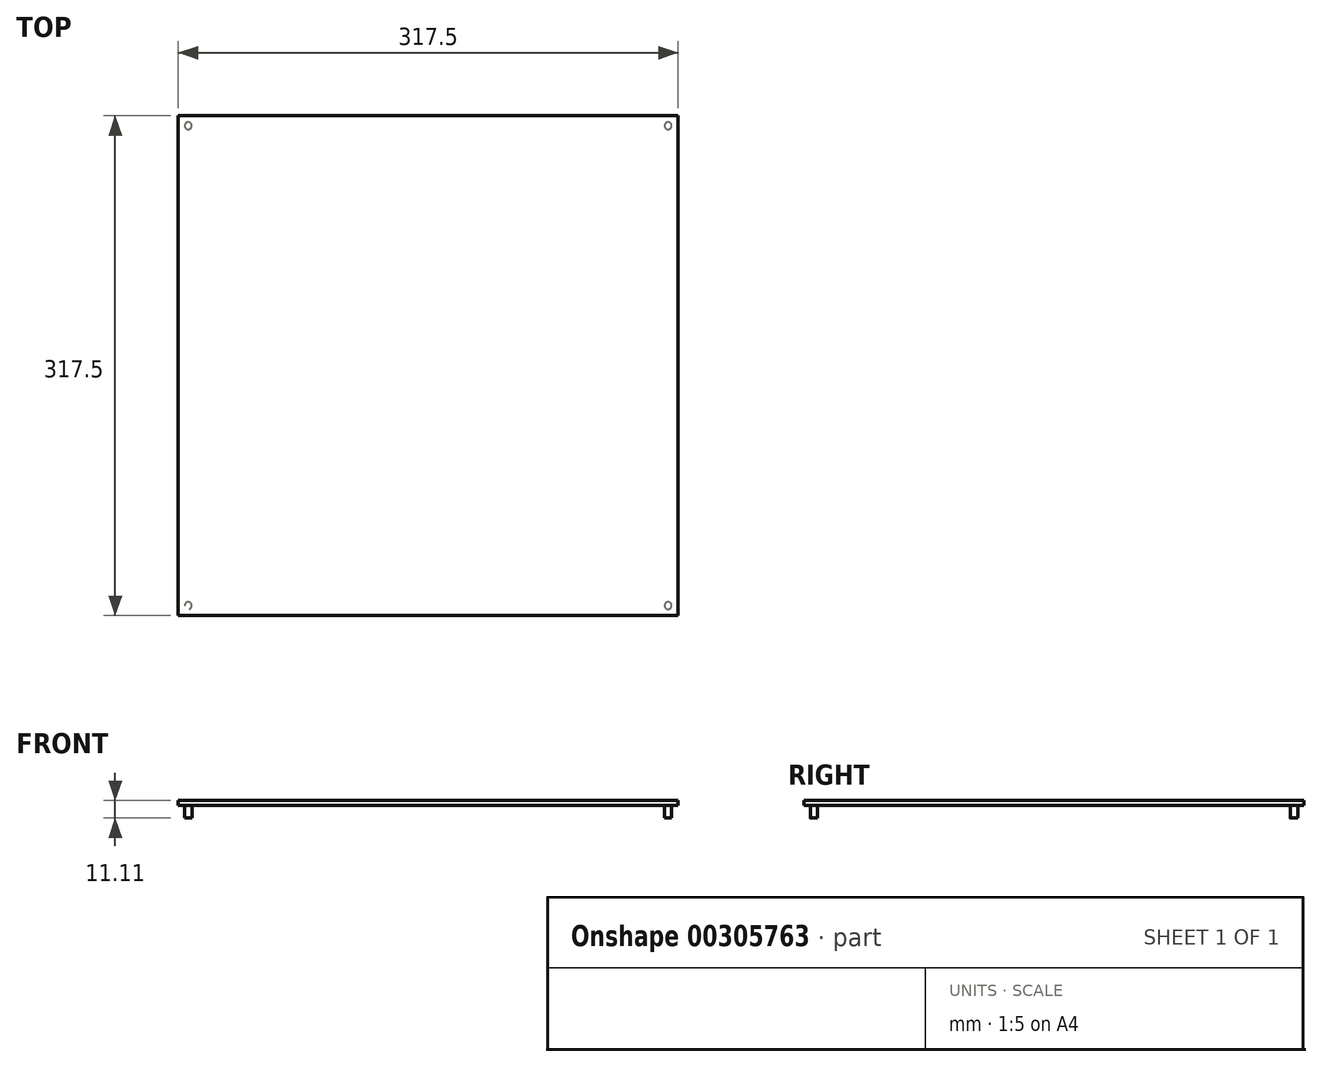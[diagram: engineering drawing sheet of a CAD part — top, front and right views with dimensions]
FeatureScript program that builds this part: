
annotation { "Feature Type Name" : "Feature", "Feature Type Description" : "" }
export const myFeature = defineFeature(function(context is Context, id is Id, definition is map)
    precondition{}
    {
        {
            var Q0;
            Q0=qCreatedBy(makeId("Top.planeOp"),FACE);
            var sketch = newSketch(context, id + "F0", { "sketchPlane" : qUnion([Q0])});
            skLineSegment(sketch, "E0.bottom", {"start": v(-158.75, 158.75) * mm, "end": v(158.75, 158.75) * mm});
            skLineSegment(sketch, "E0.top", {"start": v(-158.75, -158.75) * mm, "end": v(158.75, -158.75) * mm});
            skLineSegment(sketch, "E0.left", {"start": v(-158.75, 158.75) * mm, "end": v(-158.75, -158.75) * mm});
            skLineSegment(sketch, "E0.right", {"start": v(158.75, 158.75) * mm, "end": v(158.75, -158.75) * mm});
            skSolve(sketch);
        }
        {
            var Q0;
            Q0=makeQuery(id+"F0.imprint","IMPRINT",FACE,{"disambiguationData":[TD([[makeQuery(id+"F0.imprint","IMPRINT",EDGE,{"derivedFrom":sQuery(id+"F0.wireOp",EDGE,"E0.bottom")}),-1.0]])]});
            extrude(context, id + "F1", {"entities" : qUnion([Q0]), "depth" : 3.17 * mm});
        }
        {
            var Q0;
            Q0=makeQuery(id+"F1.opExtrude","CAP_FACE",FACE,{"disambiguationData":[OSD([sQuery(id+"F0.wireOp",EDGE,"E0.bottom"),sQuery(id+"F0.wireOp",EDGE,"E0.top"),sQuery(id+"F0.wireOp",EDGE,"E0.left"),sQuery(id+"F0.wireOp",EDGE,"E0.right")])],"isStart":true});
            var sketch = newSketch(context, id + "F2", { "sketchPlane" : qUnion([Q0])});
            skCircle(sketch, "E1", {"center": v(-152.4, 152.4) * mm, "radius": 2.31 * mm});
            skCircle(sketch, "E2", {"center": v(152.4, 152.4) * mm, "radius": 2.31 * mm});
            skCircle(sketch, "E3", {"center": v(152.4, -152.4) * mm, "radius": 2.31 * mm});
            skCircle(sketch, "E4", {"center": v(-152.4, -152.4) * mm, "radius": 2.31 * mm});
            skSolve(sketch);
        }
        {
            var Q0;
            Q0=qSketchRegion(id+"F2",true);
            extrude(context, id + "F3", {"entities" : qUnion([Q0]), "operationType" : NewBodyOperationType.ADD, "depth" : 7.94 * mm});
        }
    });
